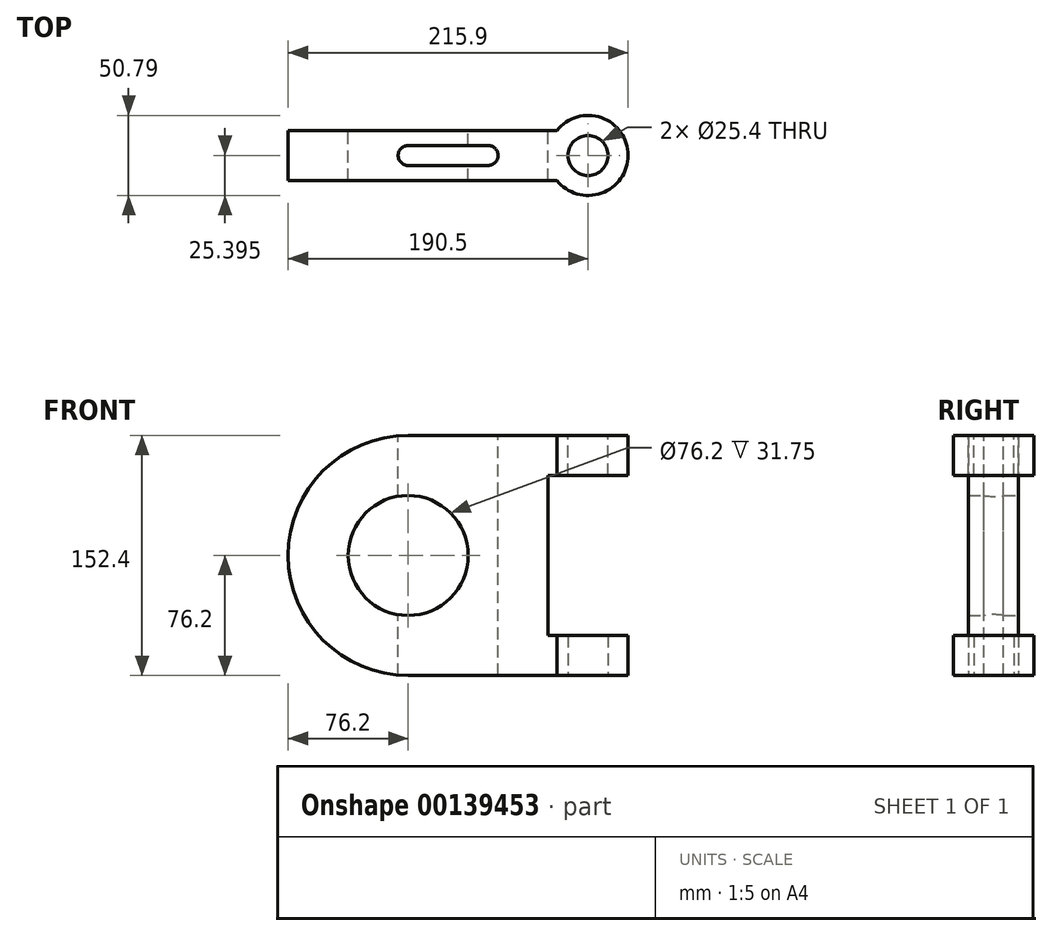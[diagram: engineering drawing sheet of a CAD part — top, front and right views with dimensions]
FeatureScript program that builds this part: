
annotation { "Feature Type Name" : "Feature", "Feature Type Description" : "" }
export const myFeature = defineFeature(function(context is Context, id is Id, definition is map)
    precondition{}
    {
        {
            var Q0;
            Q0=qCreatedBy(makeId("Front.planeOp"),FACE);
            var sketch = newSketch(context, id + "F0", { "sketchPlane" : qUnion([Q0])});
            skCircle(sketch, "E0", {"center": v(0, 0) * mm, "radius": 38.1 * mm});
            skArc(sketch, "E1", {"start": v(0, 76.2) * mm, "mid": v(-76.2, 0) * mm, "end": v(0, -76.2) * mm});
            skLineSegment(sketch, "E2", {"start": v(0, 76.2) * mm, "end": v(101.6, 76.2) * mm});
            skPoint(sketch, "E3.end.orphan", {"position": v(285.5, 0) * mm});
            skLineSegment(sketch, "E4", {"start": v(101.6, 76.2) * mm, "end": v(101.6, 50.8) * mm});
            skLineSegment(sketch, "E5", {"start": v(101.6, 50.8) * mm, "end": v(88.9, 50.8) * mm});
            skLineSegment(sketch, "E6", {"start": v(88.9, 50.8) * mm, "end": v(88.9, -50.8) * mm});
            skLineSegment(sketch, "E7", {"start": v(88.9, -50.8) * mm, "end": v(101.6, -50.8) * mm});
            skLineSegment(sketch, "E8", {"start": v(101.6, -50.8) * mm, "end": v(101.6, -76.2) * mm});
            skPoint(sketch, "E9.start.orphan", {"position": v(0, -76.2) * mm});
            skLineSegment(sketch, "E10", {"start": v(101.6, -76.2) * mm, "end": v(0, -76.2) * mm});
            skLineSegment(sketch, "E11", {"start": v(-76.2, 0) * mm, "end": v(101.6, 0) * mm});
            skSolve(sketch);
        }
        {
            var Q0;
            Q0 = qSketchRegion(id + "F0", true);
            extrude(context, id + "F1", {"entities" : qUnion([Q0]), "depth" : 31.75 * mm});
        }
        {
            var Q0;
            Q0=makeQuery(id+"F1.opExtrude","SWEPT_FACE",FACE,{"disambiguationData":[OSD([sQuery(id+"F0.wireOp",EDGE,"E2")])]});
            cPlane(context, id + "F2", {"entities" : qUnion([Q0]), "cplaneType" : CPlaneType.OFFSET, "offset" : 0 * mm, "width" : 152.4 * mm, "height" : 152.4 * mm});
        }
        {
            var Q0;
            Q0=qCreatedBy(id+"F2.planeOp",FACE);
            var sketch = newSketch(context, id + "F3", { "sketchPlane" : qUnion([Q0])});
            skCircle(sketch, "E12", {"center": v(0, -15.88) * mm, "radius": 6.35 * mm});
            skLineSegment(sketch, "E13", {"start": v(0, -9.53) * mm, "end": v(50.8, -9.53) * mm});
            skCircle(sketch, "E14", {"center": v(50.8, -15.88) * mm, "radius": 6.35 * mm});
            skLineSegment(sketch, "E15", {"start": v(0, -22.23) * mm, "end": v(50.8, -22.23) * mm});
            skCircle(sketch, "E16", {"center": v(114.3, -15.87) * mm, "radius": 12.7 * mm});
            skCircle(sketch, "E17", {"center": v(114.3, -15.87) * mm, "radius": 25.4 * mm});
            skSolve(sketch);
        }
        {
            var Q0;
            Q0=makeQuery(id+"F3.imprint","IMPRINT",FACE,{"disambiguationData":[TD([[makeQuery(id+"F3.imprint","IMPRINT",EDGE,{"derivedFrom":sQuery(id+"F3.wireOp",EDGE,"E16")}),-1.0]])]});
            extrude(context, id + "F4", {"entities" : qUnion([Q0]), "operationType" : NewBodyOperationType.ADD, "oppositeDirection" : true, "depth" : 25.4 * mm});
        }
        {
            var Q0;
            Q0=makeQuery(id+"F1.opExtrude","SWEPT_BODY",BODY,{"disambiguationData":[OSD([sQuery(id+"F0.wireOp",EDGE,"E0"),sQuery(id+"F0.wireOp",EDGE,"E1"),sQuery(id+"F0.wireOp",EDGE,"E2"),sQuery(id+"F0.wireOp",EDGE,"E4"),sQuery(id+"F0.wireOp",EDGE,"E5"),sQuery(id+"F0.wireOp",EDGE,"E6"),sQuery(id+"F0.wireOp",EDGE,"E7"),sQuery(id+"F0.wireOp",EDGE,"E8"),sQuery(id+"F0.wireOp",EDGE,"E10")])]});
            var Q1;
            Q1=qCreatedBy(makeId("Top.planeOp"),FACE);
            mirror(context, id + "F5", {"operationType" : NewBodyOperationType.ADD, "entities" : qUnion([Q0]), "mirrorPlane" : qUnion([Q1])});
        }
        {
            var Q0;
            {var subQ0=sQuery(id+"F3.wireOp",EDGE,"E12");var subQ1=makeQuery(id+"F3.imprint","INTERSECT",VERTEX,{"derivedFrom":[subQ0,sQuery(id+"F3.wireOp",EDGE,"E13")]});Q0=makeQuery(id+"F3.imprint","IMPRINT",FACE,{"disambiguationData":[TD([[makeQuery(id+"F3.imprint","IMPRINT",EDGE,{"disambiguationData":[TD([[subQ1,-1.0]])],"derivedFrom":subQ0}),1.0]])]});}
            var Q1;
            {var subQ0=sQuery(id+"F3.wireOp",EDGE,"E13");Q1=makeQuery(id+"F3.imprint","IMPRINT",FACE,{"disambiguationData":[TD([[makeQuery(id+"F3.imprint","IMPRINT",EDGE,{"derivedFrom":subQ0}),-1.0]])]});}
            var Q2;
            {var subQ0=sQuery(id+"F3.wireOp",EDGE,"E14");var subQ1=makeQuery(id+"F3.imprint","INTERSECT",VERTEX,{"derivedFrom":[sQuery(id+"F3.wireOp",EDGE,"E13"),subQ0]});Q2=makeQuery(id+"F3.imprint","IMPRINT",FACE,{"disambiguationData":[TD([[makeQuery(id+"F3.imprint","IMPRINT",EDGE,{"disambiguationData":[TD([[subQ1,-1.0]])],"derivedFrom":subQ0}),1.0]])]});}
            extrude(context, id + "F6", {"entities" : qUnion([Q0, Q1, Q2]), "operationType" : NewBodyOperationType.REMOVE, "oppositeDirection" : true, "depth" : 236.77 * mm});
        }
    });
